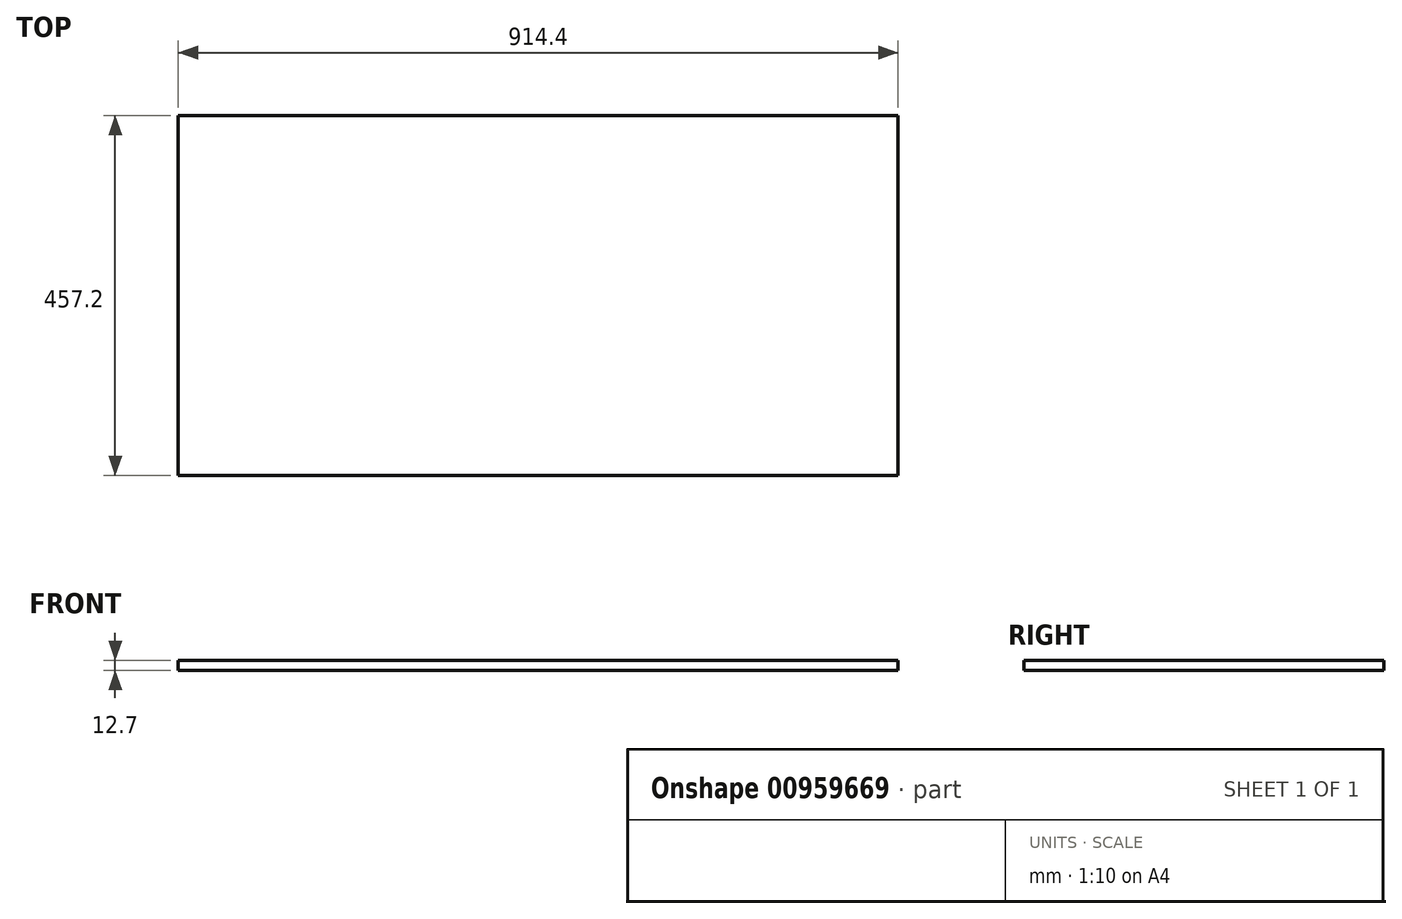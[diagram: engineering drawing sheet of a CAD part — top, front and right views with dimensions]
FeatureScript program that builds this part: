
annotation { "Feature Type Name" : "Feature", "Feature Type Description" : "" }
export const myFeature = defineFeature(function(context is Context, id is Id, definition is map)
    precondition{}
    {
        {
            var Q0;
            Q0=qCreatedBy(makeId("Top.planeOp"),FACE);
            var sketch = newSketch(context, id + "F0", { "sketchPlane" : qUnion([Q0])});
            skLineSegment(sketch, "E0.bottom", {"start": v(-402.4, 235.5) * mm, "end": v(512, 235.5) * mm});
            skLineSegment(sketch, "E0.top", {"start": v(-402.4, -221.7) * mm, "end": v(512, -221.7) * mm});
            skLineSegment(sketch, "E0.left", {"start": v(-402.4, 235.5) * mm, "end": v(-402.4, -221.7) * mm});
            skLineSegment(sketch, "E0.right", {"start": v(512, 235.5) * mm, "end": v(512, -221.7) * mm});
            skSolve(sketch);
        }
        {
            var Q0;
            Q0=makeQuery(id+"F0.imprint","IMPRINT",FACE,{"disambiguationData":[TD([[makeQuery(id+"F0.imprint","IMPRINT",EDGE,{"derivedFrom":sQuery(id+"F0.wireOp",EDGE,"E0.bottom")}),-1.0]])]});
            extrude(context, id + "F1", {"entities" : qUnion([Q0]), "depth" : 12.7 * mm, "offsetDistance" : 25.4 * mm});
        }
    });
